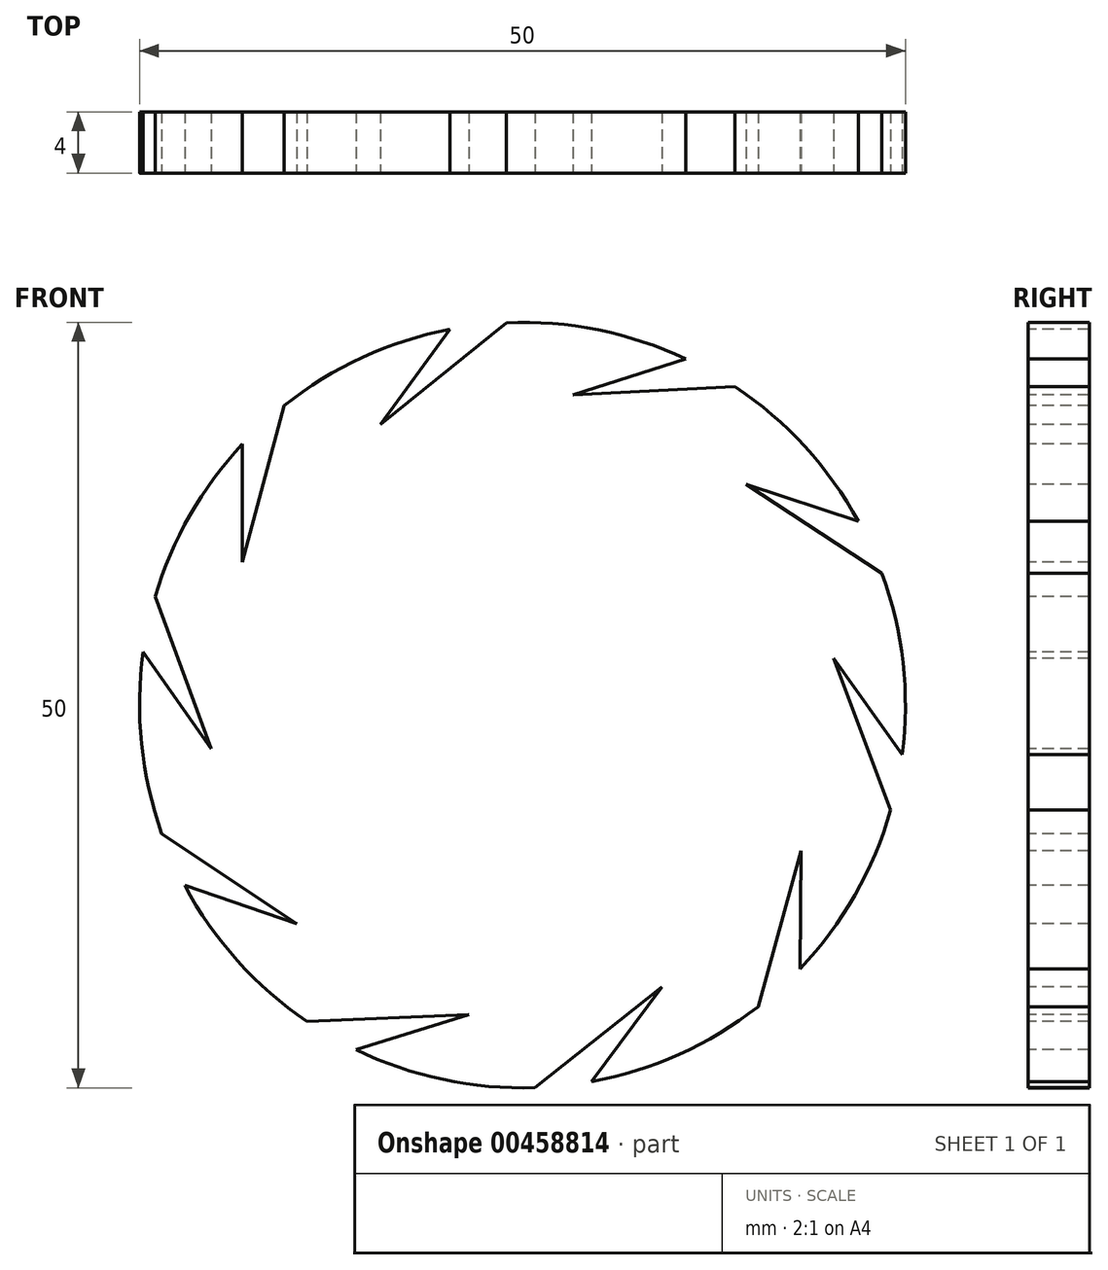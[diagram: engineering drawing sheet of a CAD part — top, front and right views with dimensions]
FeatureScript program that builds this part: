
annotation { "Feature Type Name" : "Feature", "Feature Type Description" : "" }
export const myFeature = defineFeature(function(context is Context, id is Id, definition is map)
    precondition{}
    {
        {
            var Q0;
            Q0=qCreatedBy(makeId("Front.planeOp"),FACE);
            var sketch = newSketch(context, id + "F0", { "sketchPlane" : qUnion([Q0])});
            skCircle(sketch, "E0", {"center": v(3.8, 0) * mm, "radius": 25 * mm});
            skSolve(sketch);
        }
        {
            var Q0;
            Q0=makeQuery(id+"F0.imprint","IMPRINT",FACE,{"disambiguationData":[TD([[makeQuery(id+"F0.imprint","IMPRINT",EDGE,{"derivedFrom":sQuery(id+"F0.wireOp",EDGE,"E0")}),1.0]])]});
            extrude(context, id + "F1", {"entities" : qUnion([Q0]), "depth" : 4 * mm, "offsetDistance" : 25 * mm});
        }
        {
            var Q0;
            Q0=makeQuery(id+"F1.opExtrude","CAP_FACE",FACE,{"disambiguationData":[OSD([sQuery(id+"F0.wireOp",EDGE,"E0")])],"isStart":false});
            var sketch = newSketch(context, id + "F2", { "sketchPlane" : qUnion([Q0])});
            skPoint(sketch, "E1.center", {"position": v(3.8, 0) * mm});
            skLineSegment(sketch, "E2", {"start": v(-14.48, 17.05) * mm, "end": v(-14.48, 9.33) * mm});
            skLineSegment(sketch, "E3", {"start": v(-14.48, 9.33) * mm, "end": v(-11.76, 19.56) * mm});
            skLineSegment(sketch, "E4.1.0", {"start": v(-0.92, 24.55) * mm, "end": v(-5.47, 18.31) * mm});
            skLineSegment(sketch, "E4.1.1", {"start": v(-5.47, 18.31) * mm, "end": v(2.76, 24.98) * mm});
            skLineSegment(sketch, "E4.2.0", {"start": v(14.46, 22.62) * mm, "end": v(7.1, 20.26) * mm});
            skLineSegment(sketch, "E4.2.1", {"start": v(7.1, 20.26) * mm, "end": v(17.68, 20.8) * mm});
            skLineSegment(sketch, "E4.3.0", {"start": v(25.74, 12) * mm, "end": v(18.41, 14.42) * mm});
            skLineSegment(sketch, "E4.3.1", {"start": v(18.41, 14.42) * mm, "end": v(27.27, 8.62) * mm});
            skLineSegment(sketch, "E4.4.0", {"start": v(28.6, -3.24) * mm, "end": v(24.1, 3.05) * mm});
            skLineSegment(sketch, "E4.4.1", {"start": v(24.1, 3.05) * mm, "end": v(27.85, -6.86) * mm});
            skLineSegment(sketch, "E4.5.0", {"start": v(21.93, -17.22) * mm, "end": v(22, -9.5) * mm});
            skLineSegment(sketch, "E4.5.1", {"start": v(22, -9.5) * mm, "end": v(19.19, -19.71) * mm});
            skLineSegment(sketch, "E4.6.0", {"start": v(8.3, -24.6) * mm, "end": v(12.9, -18.4) * mm});
            skLineSegment(sketch, "E4.6.1", {"start": v(12.9, -18.4) * mm, "end": v(4.62, -24.99) * mm});
            skLineSegment(sketch, "E4.7.0", {"start": v(-7.06, -22.51) * mm, "end": v(0.32, -20.23) * mm});
            skLineSegment(sketch, "E4.7.1", {"start": v(0.32, -20.23) * mm, "end": v(-10.27, -20.66) * mm});
            skLineSegment(sketch, "E4.8.0", {"start": v(-18.24, -11.78) * mm, "end": v(-10.93, -14.28) * mm});
            skLineSegment(sketch, "E4.8.1", {"start": v(-10.93, -14.28) * mm, "end": v(-19.74, -8.4) * mm});
            skLineSegment(sketch, "E4.9.0", {"start": v(-20.95, 3.48) * mm, "end": v(-16.52, -2.85) * mm});
            skLineSegment(sketch, "E4.9.1", {"start": v(-16.52, -2.85) * mm, "end": v(-20.16, 7.1) * mm});
            skLineSegment(sketch, "E4.anchor1", {"start": v(3.8, 0) * mm, "end": v(-14.48, 9.33) * mm, "construction": true});
            skLineSegment(sketch, "E4.anchor2", {"start": v(3.8, 0) * mm, "end": v(-16.52, -2.85) * mm, "construction": true});
            skSolve(sketch);
        }
        {
            var Q0;
            {var subQ0=sQuery(id+"F2.wireOp",EDGE,"E2");Q0=makeQuery(id+"F2.imprint","IMPRINT",FACE,{"disambiguationData":[TD([[makeQuery(id+"F2.imprint","IMPRINT",EDGE,{"derivedFrom":subQ0}),1.0]])]});}
            var Q1;
            {var subQ0=sQuery(id+"F2.wireOp",EDGE,"E4.1.0");Q1=makeQuery(id+"F2.imprint","IMPRINT",FACE,{"disambiguationData":[TD([[makeQuery(id+"F2.imprint","IMPRINT",EDGE,{"derivedFrom":subQ0}),1.0]])]});}
            var Q2;
            {var subQ0=sQuery(id+"F2.wireOp",EDGE,"E4.2.0");Q2=makeQuery(id+"F2.imprint","IMPRINT",FACE,{"disambiguationData":[TD([[makeQuery(id+"F2.imprint","IMPRINT",EDGE,{"derivedFrom":subQ0}),1.0]])]});}
            var Q3;
            {var subQ0=sQuery(id+"F2.wireOp",EDGE,"E4.3.0");Q3=makeQuery(id+"F2.imprint","IMPRINT",FACE,{"disambiguationData":[TD([[makeQuery(id+"F2.imprint","IMPRINT",EDGE,{"derivedFrom":subQ0}),1.0]])]});}
            var Q4;
            {var subQ0=sQuery(id+"F2.wireOp",EDGE,"E4.4.0");Q4=makeQuery(id+"F2.imprint","IMPRINT",FACE,{"disambiguationData":[TD([[makeQuery(id+"F2.imprint","IMPRINT",EDGE,{"derivedFrom":subQ0}),1.0]])]});}
            var Q5;
            {var subQ0=sQuery(id+"F2.wireOp",EDGE,"E4.5.0");Q5=makeQuery(id+"F2.imprint","IMPRINT",FACE,{"disambiguationData":[TD([[makeQuery(id+"F2.imprint","IMPRINT",EDGE,{"derivedFrom":subQ0}),1.0]])]});}
            var Q6;
            {var subQ0=sQuery(id+"F2.wireOp",EDGE,"E4.6.0");Q6=makeQuery(id+"F2.imprint","IMPRINT",FACE,{"disambiguationData":[TD([[makeQuery(id+"F2.imprint","IMPRINT",EDGE,{"derivedFrom":subQ0}),1.0]])]});}
            var Q7;
            {var subQ0=sQuery(id+"F2.wireOp",EDGE,"E4.7.0");Q7=makeQuery(id+"F2.imprint","IMPRINT",FACE,{"disambiguationData":[TD([[makeQuery(id+"F2.imprint","IMPRINT",EDGE,{"derivedFrom":subQ0}),1.0]])]});}
            var Q8;
            {var subQ0=sQuery(id+"F2.wireOp",EDGE,"E4.8.0");Q8=makeQuery(id+"F2.imprint","IMPRINT",FACE,{"disambiguationData":[TD([[makeQuery(id+"F2.imprint","IMPRINT",EDGE,{"derivedFrom":subQ0}),1.0]])]});}
            var Q9;
            {var subQ0=sQuery(id+"F2.wireOp",EDGE,"E4.9.0");Q9=makeQuery(id+"F2.imprint","IMPRINT",FACE,{"disambiguationData":[TD([[makeQuery(id+"F2.imprint","IMPRINT",EDGE,{"derivedFrom":subQ0}),1.0]])]});}
            extrude(context, id + "F3", {"entities" : qUnion([Q0, Q1, Q2, Q3, Q4, Q5, Q6, Q7, Q8, Q9]), "operationType" : NewBodyOperationType.REMOVE, "oppositeDirection" : true, "depth" : 25 * mm, "offsetDistance" : 25 * mm});
        }
    });
